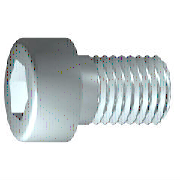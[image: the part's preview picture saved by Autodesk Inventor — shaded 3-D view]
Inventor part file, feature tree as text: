
AUTODESK INVENTOR PART (.ipt)
format: ipt  version: 2017 (Build 210142000, 142)  size: 189,952 bytes
history: native  units: mm (DEFAULTED — no unit token found)
features: sketch x2, other x1, extrude x1, plane x1
ambient origin geometry x7: Origin, YZ Plane, XY Plane, X Axis, Y Axis, Z Axis, Center Point
bodies: Solid1 (feature_tree)
feature tree (5):
  other  "Corps"
  extrude  "Rainure"  Depth=8.693275mm
  plane  "Work Plane1"
  sketch  "Esquisse1"
  sketch  "Esquisse2"
